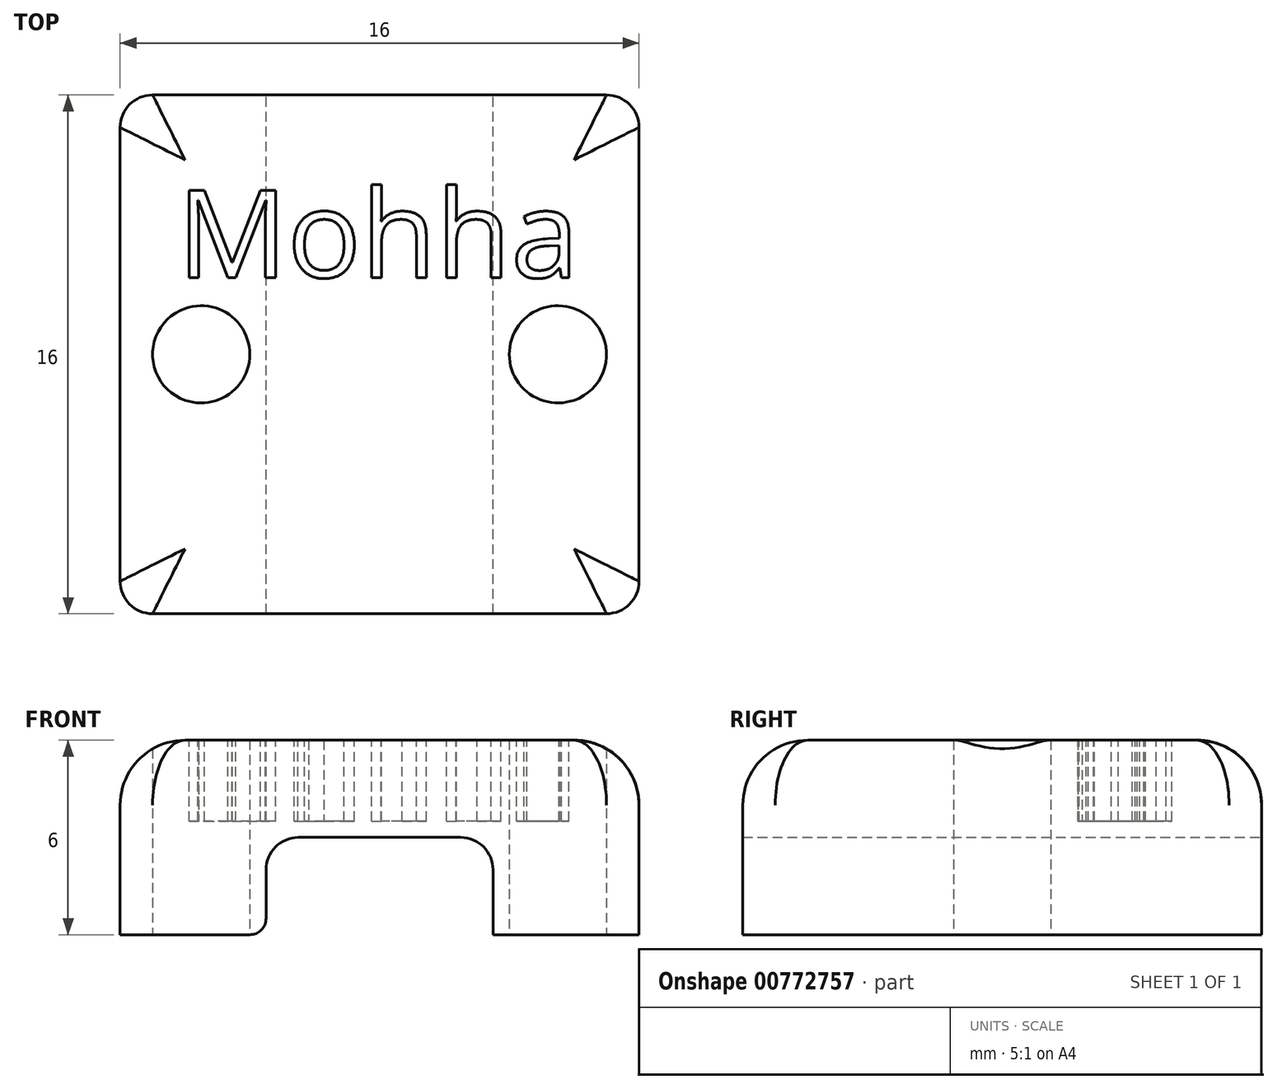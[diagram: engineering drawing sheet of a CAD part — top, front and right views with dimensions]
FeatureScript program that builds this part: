
annotation { "Feature Type Name" : "Feature", "Feature Type Description" : "" }
export const myFeature = defineFeature(function(context is Context, id is Id, definition is map)
    precondition{}
    {
        {
            var Q0;
            Q0=qCreatedBy(makeId("Top.planeOp"),FACE);
            var sketch = newSketch(context, id + "F0", { "sketchPlane" : qUnion([Q0])});
            skLineSegment(sketch, "E0.bottom", {"start": v(-8, 8) * mm, "end": v(8, 8) * mm});
            skLineSegment(sketch, "E0.top", {"start": v(-8, -8) * mm, "end": v(8, -8) * mm});
            skLineSegment(sketch, "E0.left", {"start": v(-8, 8) * mm, "end": v(-8, -8) * mm});
            skLineSegment(sketch, "E0.right", {"start": v(8, 8) * mm, "end": v(8, -8) * mm});
            skPoint(sketch, "E0.middle", {"position": v(0, 0) * mm});
            skCircle(sketch, "E1", {"center": v(-5.5, 0) * mm, "radius": 1.5 * mm});
            skCircle(sketch, "E2.MirrorC", {"center": v(5.5, 0) * mm, "radius": 1.5 * mm});
            skSolve(sketch);
        }
        {
            var Q0;
            Q0=makeQuery(id+"F0.imprint","IMPRINT",FACE,{"disambiguationData":[TD([[makeQuery(id+"F0.imprint","IMPRINT",EDGE,{"derivedFrom":sQuery(id+"F0.wireOp",EDGE,"E0.bottom")}),-1.0]])]});
            extrude(context, id + "F1", {"entities" : qUnion([Q0]), "depth" : 6 * mm, "offsetDistance" : 25 * mm});
        }
        {
            var Q0;
            Q0=makeQuery(id+"F1.opExtrude","CAP_FACE",FACE,{"disambiguationData":[OSD([sQuery(id+"F0.wireOp",EDGE,"E0.bottom"),sQuery(id+"F0.wireOp",EDGE,"E0.top"),sQuery(id+"F0.wireOp",EDGE,"E0.left"),sQuery(id+"F0.wireOp",EDGE,"E0.right"),sQuery(id+"F0.wireOp",EDGE,"E1"),sQuery(id+"F0.wireOp",EDGE,"E2.MirrorC")])],"isStart":true});
            var sketch = newSketch(context, id + "F2", { "sketchPlane" : qUnion([Q0])});
            skLineSegment(sketch, "E3.bottom", {"start": v(-3.5, 8) * mm, "end": v(3.5, 8) * mm});
            skLineSegment(sketch, "E3.top", {"start": v(-3.5, -8) * mm, "end": v(3.5, -8) * mm});
            skLineSegment(sketch, "E3.left", {"start": v(-3.5, 8) * mm, "end": v(-3.5, -8) * mm});
            skLineSegment(sketch, "E3.right", {"start": v(3.5, 8) * mm, "end": v(3.5, -8) * mm});
            skSolve(sketch);
        }
        {
            var Q0;
            Q0=makeQuery(id+"F2.imprint","IMPRINT",FACE,{"disambiguationData":[TD([[makeQuery(id+"F2.imprint","IMPRINT",EDGE,{"derivedFrom":sQuery(id+"F2.wireOp",EDGE,"E3.bottom")}),-1.0]])]});
            extrude(context, id + "F3", {"entities" : qUnion([Q0]), "operationType" : NewBodyOperationType.REMOVE, "oppositeDirection" : true, "depth" : 3 * mm, "offsetDistance" : 25 * mm});
        }
        {
            var Q0;
            Q0=makeQuery(id+"F1.opExtrude","CAP_EDGE",EDGE,{"disambiguationData":[OSD([sQuery(id+"F0.wireOp",EDGE,"E0.left")])],"isStart":false});
            var Q1;
            Q1=makeQuery(id+"F1.opExtrude","CAP_EDGE",EDGE,{"disambiguationData":[OSD([sQuery(id+"F0.wireOp",EDGE,"E0.right")])],"isStart":false});
            var Q2;
            Q2=makeQuery(id+"F1.opExtrude","CAP_EDGE",EDGE,{"disambiguationData":[OSD([sQuery(id+"F0.wireOp",EDGE,"E0.bottom")])],"isStart":false});
            var Q3;
            Q3=makeQuery(id+"F1.opExtrude","CAP_EDGE",EDGE,{"disambiguationData":[OSD([sQuery(id+"F0.wireOp",EDGE,"E0.top")])],"isStart":false});
            fillet(context, id + "F4", {"entities" : qUnion([Q0, Q1, Q2, Q3]), "radius" : 2 * mm, "tangentPropagation" : true, "allowEdgeOverflow" : false});
        }
        {
            var Q0;
            Q0=makeQuery(id+"F1.opExtrude","CAP_FACE",FACE,{"disambiguationData":[OSD([sQuery(id+"F0.wireOp",EDGE,"E0.bottom"),sQuery(id+"F0.wireOp",EDGE,"E0.top"),sQuery(id+"F0.wireOp",EDGE,"E0.left"),sQuery(id+"F0.wireOp",EDGE,"E0.right"),sQuery(id+"F0.wireOp",EDGE,"E1"),sQuery(id+"F0.wireOp",EDGE,"E2.MirrorC")])],"isStart":false});
            var sketch = newSketch(context, id + "F5", { "sketchPlane" : qUnion([Q0])});
            skText(sketch, "E4", { "text": "Mohha", "fontName": "OpenSans-Regular.ttf"});
            const initialGuessF5  = {"E4": [-0.00624, 0.00237, 1, 0, 0.00271]};
            skSetInitialGuess(sketch, initialGuessF5);
            skSolve(sketch);
        }
        {
            var Q0;
            Q0 = qSketchRegion(id + "F5", true);
            extrude(context, id + "F6", {"entities" : qUnion([Q0]), "operationType" : NewBodyOperationType.REMOVE, "oppositeDirection" : true, "depth" : 2.5 * mm, "offsetDistance" : 25 * mm});
        }
        {
            var Q0;
            Q0=makeQuery(id+"F3.boolean.opBoolean","COPY",EDGE,{"derivedFrom":makeQuery(id+"F3.opExtrude","CAP_EDGE",EDGE,{"disambiguationData":[OSD([sQuery(id+"F2.wireOp",EDGE,"E3.left")])],"isStart":false})});
            var Q1;
            Q1=makeQuery(id+"F3.boolean.opBoolean","COPY",EDGE,{"derivedFrom":makeQuery(id+"F3.opExtrude","CAP_EDGE",EDGE,{"disambiguationData":[OSD([sQuery(id+"F2.wireOp",EDGE,"E3.right")])],"isStart":false})});
            fillet(context, id + "F7", {"entities" : qUnion([Q0, Q1]), "radius" : 1 * mm, "tangentPropagation" : true, "allowEdgeOverflow" : false});
        }
        {
            var Q0;
            Q0=makeQuery(id+"F4.opFillet","BLEND_EDGE",EDGE,{"blendedFrom":[makeQuery(id+"F1.opExtrude","CAP_EDGE",EDGE,{"disambiguationData":[OSD([sQuery(id+"F0.wireOp",EDGE,"E0.top")])],"isStart":false}),makeQuery(id+"F1.opExtrude","CAP_EDGE",EDGE,{"disambiguationData":[OSD([sQuery(id+"F0.wireOp",EDGE,"E0.right")])],"isStart":false})],"blendedInto":[]});
            var Q1;
            Q1=makeQuery(id+"F4.opFillet","BLEND_EDGE",EDGE,{"blendedFrom":[makeQuery(id+"F1.opExtrude","CAP_EDGE",EDGE,{"disambiguationData":[OSD([sQuery(id+"F0.wireOp",EDGE,"E0.top")])],"isStart":false}),makeQuery(id+"F1.opExtrude","CAP_EDGE",EDGE,{"disambiguationData":[OSD([sQuery(id+"F0.wireOp",EDGE,"E0.left")])],"isStart":false})],"blendedInto":[]});
            var Q2;
            Q2=makeQuery(id+"F4.opFillet","BLEND_EDGE",EDGE,{"blendedFrom":[makeQuery(id+"F1.opExtrude","CAP_EDGE",EDGE,{"disambiguationData":[OSD([sQuery(id+"F0.wireOp",EDGE,"E0.bottom")])],"isStart":false}),makeQuery(id+"F1.opExtrude","CAP_EDGE",EDGE,{"disambiguationData":[OSD([sQuery(id+"F0.wireOp",EDGE,"E0.left")])],"isStart":false})],"blendedInto":[]});
            var Q3;
            Q3=makeQuery(id+"F4.opFillet","BLEND_EDGE",EDGE,{"blendedFrom":[makeQuery(id+"F1.opExtrude","CAP_EDGE",EDGE,{"disambiguationData":[OSD([sQuery(id+"F0.wireOp",EDGE,"E0.bottom")])],"isStart":false}),makeQuery(id+"F1.opExtrude","CAP_EDGE",EDGE,{"disambiguationData":[OSD([sQuery(id+"F0.wireOp",EDGE,"E0.right")])],"isStart":false})],"blendedInto":[]});
            fillet(context, id + "F8", {"entities" : qUnion([Q0, Q1, Q2, Q3]), "radius" : 1 * mm, "tangentPropagation" : true, "allowEdgeOverflow" : false});
        }
        {
            var Q0;
            Q0=makeQuery(id+"F3.boolean.opBoolean","COPY",EDGE,{"derivedFrom":makeQuery(id+"F3.opExtrude","CAP_EDGE",EDGE,{"disambiguationData":[OSD([sQuery(id+"F2.wireOp",EDGE,"E3.right")])],"isStart":true})});
            var Q1;
            Q1=makeQuery(id+"F3.boolean.opBoolean","COPY",EDGE,{"derivedFrom":makeQuery(id+"F3.opExtrude","CAP_EDGE",EDGE,{"disambiguationData":[OSD([sQuery(id+"F2.wireOp",EDGE,"E3.left")])],"isStart":true})});
            fillet(context, id + "F9", {"entities" : qUnion([Q0, Q1]), "radius" : 0.5 * mm, "tangentPropagation" : true, "allowEdgeOverflow" : false});
        }
    });
